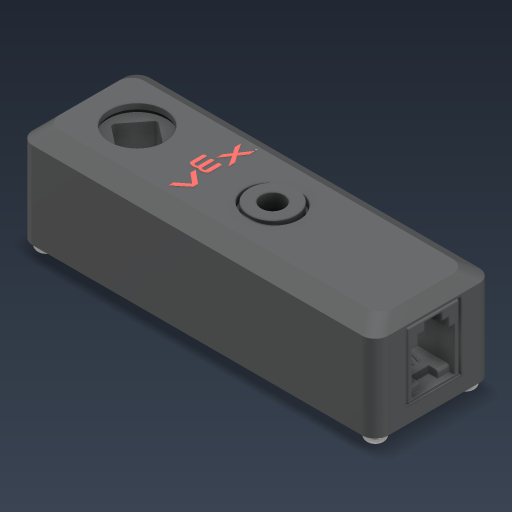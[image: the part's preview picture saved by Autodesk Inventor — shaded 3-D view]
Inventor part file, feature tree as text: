
AUTODESK INVENTOR PART (.ipt)
format: ipt  version: 2023 (Build 270158000, 158)  size: 3,027,456 bytes
history: native  units: in
note: dims shown in document units (in); Inventor stores cm internally (conversion verified against a paired STEP export)
features: other x11, extrude x1, sketch x1
ambient origin geometry x8: Origin, YZ Plane, XZ Plane, XY Plane, X Axis, Y Axis, Z Axis, Center Point
bodies: Solid1 (feature_tree), Solid2 (feature_tree), Solid3 (feature_tree), Solid4 (feature_tree), Solid5 (feature_tree), Solid6 (feature_tree), Solid7 (feature_tree), Solid8 (feature_tree), Solid9 (feature_tree), Solid10 (feature_tree)
feature tree (13):
  other  "V5 Rotation Sensor.iam"
  other  "276-6050-001 Web.ipt:1"
  other  "276-6050-002 Web.ipt:1"
  other  "276-6050-005 Web.ipt:1"
  other  "276-6050-015 Web.ipt:1"
  other  "276-6050-019 Web.ipt:1"
  other  "276-6050-901 Web.ipt:1"
  other  "276-6050-019 Web.ipt:2"
  other  "276-6050-019 Web.ipt:3"
  other  "276-6050-019 Web.ipt:4"
  other  "276-6050-013 Web_276-6050-013 Rev6.ipt:1"
  extrude  "Extrusion1"  Depth=0.3937in TaperAngle=0.0deg
  sketch  "Sketch1"  dims[d0=0.3937in d10=0.002in d11=0.0in]
